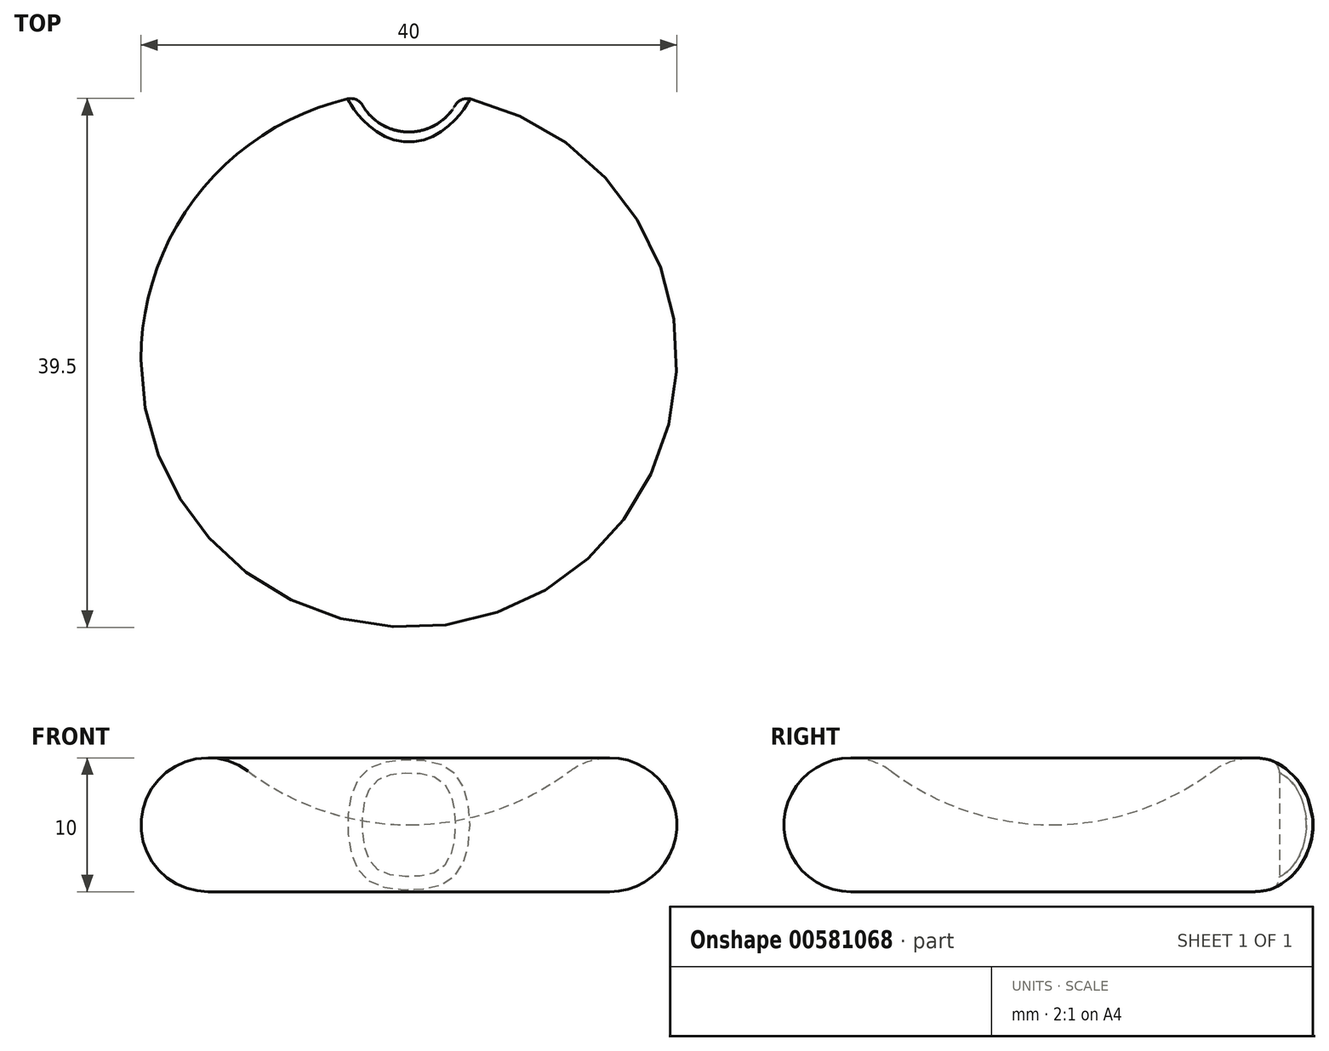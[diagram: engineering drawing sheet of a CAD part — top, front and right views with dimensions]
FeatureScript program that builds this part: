
annotation { "Feature Type Name" : "Feature", "Feature Type Description" : "" }
export const myFeature = defineFeature(function(context is Context, id is Id, definition is map)
    precondition{}
    {
        {
            var Q0;
            Q0=qCreatedBy(makeId("Front.planeOp"),FACE);
            var sketch = newSketch(context, id + "F0", { "sketchPlane" : qUnion([Q0])});
            skArc(sketch, "E0", {"start": v(-12, 9) * mm, "mid": v(-19.74, 6.58) * mm, "end": v(-15, 0) * mm});
            skArc(sketch, "E1", {"start": v(-12, 9) * mm, "mid": v(-6.32, 6.03) * mm, "end": v(0, 5) * mm});
            skLineSegment(sketch, "E2", {"start": v(0, 0) * mm, "end": v(-15, 0) * mm});
            skLineSegment(sketch, "E3", {"start": v(0, 0) * mm, "end": v(0, 5) * mm});
            skSolve(sketch);
        }
        {
            var Q0;
            Q0 = qSketchRegion(id + "F0", true);
            var Q1;
            Q1=sQuery(id+"F0.wireOp",EDGE,"E3");
            revolve(context, id + "F1", {"entities" : qUnion([Q0]), "axis" : qUnion([Q1]), "revolveType" : RevolveType.FULL});
        }
        {
            var Q0;
            Q0=qCreatedBy(makeId("Front.planeOp"),FACE);
            var sketch = newSketch(context, id + "F2", { "sketchPlane" : qUnion([Q0])});
            skCircle(sketch, "E4", {"center": v(-15, 5) * mm, "radius": 4 * mm});
            skSolve(sketch);
        }
        {
            var Q0;
            Q0 = qSketchRegion(id + "F2", true);
            var Q1;
            Q1=sQuery(id+"F0.wireOp",EDGE,"E3");
            revolve(context, id + "F3", {"operationType" : NewBodyOperationType.ADD, "entities" : qUnion([Q0]), "axis" : qUnion([Q1]), "revolveType" : RevolveType.FULL});
        }
        {
            var Q0;
            Q0=qCreatedBy(makeId("Top.planeOp"),FACE);
            var sketch = newSketch(context, id + "F4", { "sketchPlane" : qUnion([Q0])});
            skCircle(sketch, "E5", {"center": v(0, 21) * mm, "radius": 4 * mm});
            skSolve(sketch);
        }
        {
            var Q0;
            Q0=makeQuery(id+"F4.imprint","IMPRINT",FACE,{"disambiguationData":[TD([[makeQuery(id+"F4.imprint","IMPRINT",EDGE,{"derivedFrom":sQuery(id+"F4.wireOp",EDGE,"E5")}),1.0]])]});
            var Q1;
            Q1 = qSketchRegion(id + "F4", true);
            extrude(context, id + "F5", {"entities" : qUnion([Q0, Q1]), "operationType" : NewBodyOperationType.REMOVE, "depth" : 25 * mm, "offsetDistance" : 25 * mm});
        }
        {
            var Q0;
            Q0=makeQuery(id+"F5.boolean.opBoolean","INTERSECT",EDGE,{"derivedFrom":[makeQuery(id+"F1.opRevolve","SWEPT_FACE",FACE,{"disambiguationData":[OSD([sQuery(id+"F0.wireOp",EDGE,"E0")])]}),makeQuery(id+"F5.opExtrude","SWEPT_FACE",FACE,{"disambiguationData":[OSD([sQuery(id+"F4.wireOp",EDGE,"E5")])]})]});
            fillet(context, id + "F6", {"entities" : qUnion([Q0]), "radius" : 1 * mm, "tangentPropagation" : true, "allowEdgeOverflow" : false});
        }
    });
